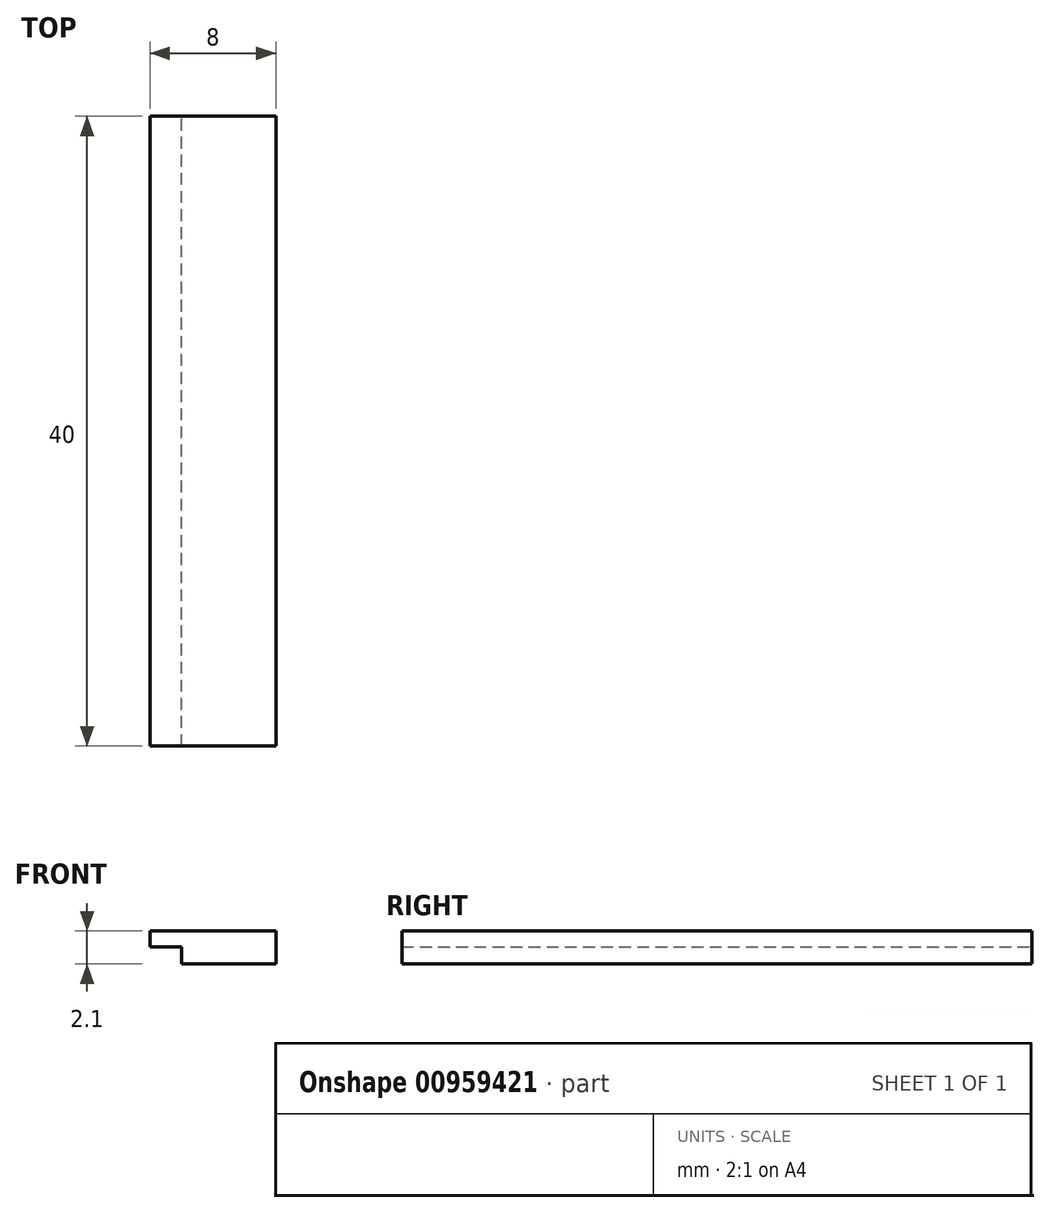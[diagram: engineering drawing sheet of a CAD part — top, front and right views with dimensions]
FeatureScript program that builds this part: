
annotation { "Feature Type Name" : "Feature", "Feature Type Description" : "" }
export const myFeature = defineFeature(function(context is Context, id is Id, definition is map)
    precondition{}
    {
        {
            var Q0;
            Q0=qCreatedBy(makeId("Front.planeOp"),FACE);
            var sketch = newSketch(context, id + "F0", { "sketchPlane" : qUnion([Q0])});
            skLineSegment(sketch, "E0", {"start": v(3.5, 2.1) * mm, "end": v(-4.5, 2.1) * mm});
            skLineSegment(sketch, "E1", {"start": v(-4.5, 2.1) * mm, "end": v(-4.5, 1.1) * mm});
            skLineSegment(sketch, "E2", {"start": v(-4.5, 1.1) * mm, "end": v(-2.5, 1.1) * mm});
            skLineSegment(sketch, "E3", {"start": v(-2.5, 1.1) * mm, "end": v(-2.5, 0) * mm});
            skLineSegment(sketch, "E4", {"start": v(-2.5, 0) * mm, "end": v(3.5, 0) * mm});
            skLineSegment(sketch, "E5", {"start": v(3.5, 2.1) * mm, "end": v(3.5, 0) * mm});
            skLineSegment(sketch, "E6", {"start": v(0, 0) * mm, "end": v(-2.5, 0) * mm});
            skSolve(sketch);
        }
        {
            var Q0;
            Q0=makeQuery(id+"F0.imprint","IMPRINT",FACE,{"disambiguationData":[TD([[makeQuery(id+"F0.imprint","IMPRINT",EDGE,{"derivedFrom":sQuery(id+"F0.wireOp",EDGE,"E0")}),1.0]])]});
            var Q1;
            Q1=makeQuery(id+"F0.imprint","IMPRINT",FACE,{"disambiguationData":[TD([[makeQuery(id+"F0.imprint","IMPRINT",EDGE,{"derivedFrom":sQuery(id+"F0.wireOp",EDGE,"E4")}),-1.0]])]});
            extrude(context, id + "F1", {"entities" : qUnion([Q0, Q1]), "endBound" : BoundingType.SYMMETRIC, "depth" : 40 * mm, "offsetDistance" : 25 * mm});
        }
    });
